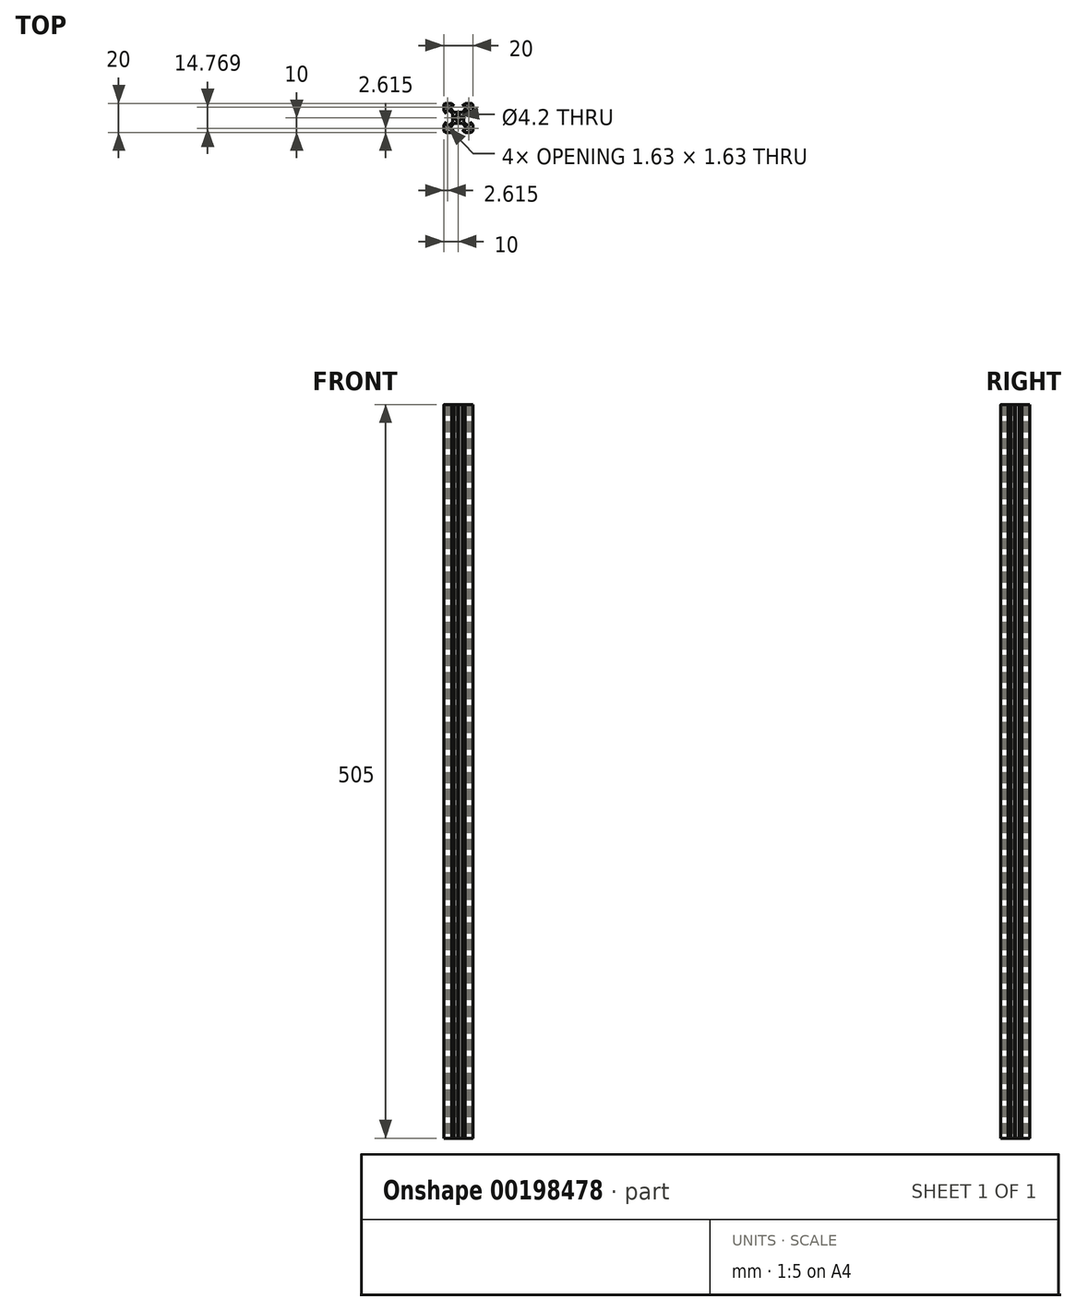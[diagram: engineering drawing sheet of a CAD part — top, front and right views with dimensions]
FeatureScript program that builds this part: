
annotation { "Feature Type Name" : "Feature", "Feature Type Description" : "" }
export const myFeature = defineFeature(function(context is Context, id is Id, definition is map)
    precondition{}
    {
        {
            var Q0;
            Q0=qCreatedBy(makeId("Top.planeOp"),FACE);
            var sketch = newSketch(context, id + "F0", { "sketchPlane" : qUnion([Q0])});
            skLineSegment(sketch, "E0", {"start": v(10, 8.5) * mm, "end": v(10, 4.64) * mm});
            skLineSegment(sketch, "E1", {"start": v(8.5, -10) * mm, "end": v(4.64, -10) * mm});
            skLineSegment(sketch, "E2", {"start": v(-10, -8.5) * mm, "end": v(-10, -4.64) * mm});
            skLineSegment(sketch, "E3", {"start": v(-8.5, 10) * mm, "end": v(-4.64, 10) * mm});
            skLineSegment(sketch, "E4.0", {"start": v(-5.5, 8.2) * mm, "end": v(-2.84, 8.2) * mm});
            skLineSegment(sketch, "E4.1", {"start": v(-8.2, -5.5) * mm, "end": v(-8.2, -2.84) * mm});
            skLineSegment(sketch, "E4.2", {"start": v(5.5, -8.2) * mm, "end": v(2.84, -8.2) * mm});
            skLineSegment(sketch, "E4.3", {"start": v(8.2, 5.5) * mm, "end": v(8.2, 2.84) * mm});
            skLineSegment(sketch, "E5.trimOffspring", {"start": v(4.64, 10) * mm, "end": v(8.5, 10) * mm});
            skPoint(sketch, "E6.start.orphan", {"position": v(0, 10) * mm});
            skLineSegment(sketch, "E7", {"start": v(-2.84, 8.2) * mm, "end": v(-4.64, 10) * mm});
            skLineSegment(sketch, "E8.trimOffspring", {"start": v(2.84, 8.2) * mm, "end": v(5.5, 8.2) * mm});
            skLineSegment(sketch, "E9.MirrorCS", {"start": v(2.84, 8.2) * mm, "end": v(4.64, 10) * mm});
            skLineSegment(sketch, "E10.MirrorCS", {"start": v(2.84, -8.2) * mm, "end": v(4.64, -10) * mm});
            skLineSegment(sketch, "E11.MirrorCS", {"start": v(-2.84, -8.2) * mm, "end": v(-4.64, -10) * mm});
            skLineSegment(sketch, "E12.trimOffspring", {"start": v(-2.84, -8.2) * mm, "end": v(-5.5, -8.2) * mm});
            skLineSegment(sketch, "E13.trimOffspring", {"start": v(-4.64, -10) * mm, "end": v(-8.5, -10) * mm});
            skLineSegment(sketch, "E14", {"start": v(-8.2, 2.84) * mm, "end": v(-10, 4.64) * mm});
            skLineSegment(sketch, "E15", {"start": v(-8.2, -2.84) * mm, "end": v(-10, -4.64) * mm});
            skLineSegment(sketch, "E16.trimOffspring", {"start": v(-10, 4.64) * mm, "end": v(-10, 8.5) * mm});
            skLineSegment(sketch, "E17.trimOffspring", {"start": v(-8.2, 2.84) * mm, "end": v(-8.2, 5.5) * mm});
            skLineSegment(sketch, "E18.MirrorCS", {"start": v(8.2, 2.84) * mm, "end": v(10, 4.64) * mm});
            skLineSegment(sketch, "E19.MirrorCS", {"start": v(8.2, -2.84) * mm, "end": v(10, -4.64) * mm});
            skLineSegment(sketch, "E20.trimOffspring", {"start": v(8.2, -2.84) * mm, "end": v(8.2, -5.5) * mm});
            skLineSegment(sketch, "E21.trimOffspring", {"start": v(10, -4.64) * mm, "end": v(10, -8.5) * mm});
            skCircle(sketch, "E22", {"center": v(0, 0) * mm, "radius": 2.1 * mm});
            skLineSegment(sketch, "E23", {"start": v(-6.56, 5.5) * mm, "end": v(-3.9, 2.84) * mm});
            skLineSegment(sketch, "E24", {"start": v(-5.5, 6.56) * mm, "end": v(-2.84, 3.9) * mm});
            skLineSegment(sketch, "E25", {"start": v(-5.5, 6.56) * mm, "end": v(-5.5, 8.2) * mm});
            skLineSegment(sketch, "E26", {"start": v(-6.56, 5.5) * mm, "end": v(-8.2, 5.5) * mm});
            skLineSegment(sketch, "E27", {"start": v(6.56, 5.5) * mm, "end": v(3.9, 2.84) * mm});
            skLineSegment(sketch, "E28", {"start": v(5.5, 6.56) * mm, "end": v(2.84, 3.9) * mm});
            skLineSegment(sketch, "E29", {"start": v(-6.56, -5.5) * mm, "end": v(-8.2, -5.5) * mm});
            skLineSegment(sketch, "E30", {"start": v(-5.5, -6.56) * mm, "end": v(-5.5, -8.2) * mm});
            skLineSegment(sketch, "E31", {"start": v(5.5, 6.56) * mm, "end": v(5.5, 8.2) * mm});
            skLineSegment(sketch, "E32", {"start": v(6.56, 5.5) * mm, "end": v(8.2, 5.5) * mm});
            skLineSegment(sketch, "E33", {"start": v(5.5, -6.56) * mm, "end": v(5.5, -8.2) * mm});
            skLineSegment(sketch, "E34", {"start": v(6.56, -5.5) * mm, "end": v(8.2, -5.5) * mm});
            skLineSegment(sketch, "E35.trimOffspring", {"start": v(2.84, -3.9) * mm, "end": v(5.5, -6.56) * mm});
            skLineSegment(sketch, "E36.trimOffspring", {"start": v(-2.84, -3.9) * mm, "end": v(-5.5, -6.56) * mm});
            skLineSegment(sketch, "E37.trimOffspring", {"start": v(-3.9, -2.84) * mm, "end": v(-6.56, -5.5) * mm});
            skLineSegment(sketch, "E38.trimOffspring", {"start": v(3.9, -2.84) * mm, "end": v(6.56, -5.5) * mm});
            skLineSegment(sketch, "E39", {"start": v(-3.9, -2.84) * mm, "end": v(-3.9, -0.25) * mm});
            skLineSegment(sketch, "E40", {"start": v(-2.84, 3.9) * mm, "end": v(-0.25, 3.9) * mm});
            skLineSegment(sketch, "E41", {"start": v(-2.84, -3.9) * mm, "end": v(-0.25, -3.9) * mm});
            skLineSegment(sketch, "E42", {"start": v(3.9, 2.84) * mm, "end": v(3.9, 0.25) * mm});
            skLineSegment(sketch, "E43", {"start": v(-8.2, 6.57) * mm, "end": v(-8.2, 8.2) * mm});
            skLineSegment(sketch, "E44", {"start": v(-6.57, 8.2) * mm, "end": v(-8.2, 8.2) * mm});
            skLineSegment(sketch, "E45", {"start": v(-8.2, 6.57) * mm, "end": v(-7.63, 6.57) * mm});
            skLineSegment(sketch, "E46", {"start": v(-6.57, 8.2) * mm, "end": v(-6.57, 7.63) * mm});
            skLineSegment(sketch, "E47", {"start": v(-7.63, 6.57) * mm, "end": v(-6.57, 7.63) * mm});
            skLineSegment(sketch, "E48.MirrorCS", {"start": v(6.57, 8.2) * mm, "end": v(8.2, 8.2) * mm});
            skLineSegment(sketch, "E49.MirrorCS", {"start": v(8.2, 6.57) * mm, "end": v(8.2, 8.2) * mm});
            skLineSegment(sketch, "E50.MirrorCS", {"start": v(8.2, 6.57) * mm, "end": v(7.63, 6.57) * mm});
            skLineSegment(sketch, "E51.MirrorCS", {"start": v(7.63, 6.57) * mm, "end": v(6.57, 7.63) * mm});
            skLineSegment(sketch, "E52.MirrorCS", {"start": v(6.57, 8.2) * mm, "end": v(6.57, 7.63) * mm});
            skLineSegment(sketch, "E53.MirrorCS", {"start": v(6.57, -8.2) * mm, "end": v(6.57, -7.63) * mm});
            skLineSegment(sketch, "E54.MirrorCS", {"start": v(8.2, -6.57) * mm, "end": v(7.63, -6.57) * mm});
            skLineSegment(sketch, "E55.MirrorCS", {"start": v(7.63, -6.57) * mm, "end": v(6.57, -7.63) * mm});
            skLineSegment(sketch, "E56.MirrorCS", {"start": v(6.57, -8.2) * mm, "end": v(8.2, -8.2) * mm});
            skLineSegment(sketch, "E57.MirrorCS", {"start": v(8.2, -6.57) * mm, "end": v(8.2, -8.2) * mm});
            skLineSegment(sketch, "E58.MirrorCS", {"start": v(-6.57, -8.2) * mm, "end": v(-8.2, -8.2) * mm});
            skLineSegment(sketch, "E59.MirrorCS", {"start": v(-8.2, -6.57) * mm, "end": v(-7.63, -6.57) * mm});
            skLineSegment(sketch, "E60.MirrorCS", {"start": v(-8.2, -6.57) * mm, "end": v(-8.2, -8.2) * mm});
            skLineSegment(sketch, "E61.MirrorCS", {"start": v(-7.63, -6.57) * mm, "end": v(-6.57, -7.63) * mm});
            skLineSegment(sketch, "E62.MirrorCS", {"start": v(-6.57, -8.2) * mm, "end": v(-6.57, -7.63) * mm});
            skPoint(sketch, "E63.visualSharp", {"position": v(-10, 10) * mm});
            skArc(sketch, "E63.filletArc", {"start": v(-8.5, 10) * mm, "mid": v(-9.56, 9.56) * mm, "end": v(-10, 8.5) * mm});
            skPoint(sketch, "E64.visualSharp", {"position": v(10, 10) * mm});
            skArc(sketch, "E64.filletArc", {"start": v(10, 8.5) * mm, "mid": v(9.56, 9.56) * mm, "end": v(8.5, 10) * mm});
            skPoint(sketch, "E65.visualSharp", {"position": v(10, -10) * mm});
            skArc(sketch, "E65.filletArc", {"start": v(8.5, -10) * mm, "mid": v(9.56, -9.56) * mm, "end": v(10, -8.5) * mm});
            skPoint(sketch, "E66.visualSharp", {"position": v(-10, -10) * mm});
            skArc(sketch, "E66.filletArc", {"start": v(-10, -8.5) * mm, "mid": v(-9.56, -9.56) * mm, "end": v(-8.5, -10) * mm});
            skLineSegment(sketch, "E67", {"start": v(-3.65, 0) * mm, "end": v(-3.9, 0.25) * mm});
            skLineSegment(sketch, "E68.MirrorCS", {"start": v(-3.65, 0) * mm, "end": v(-3.9, -0.25) * mm});
            skLineSegment(sketch, "E69.trimOffspring", {"start": v(-3.9, 0.25) * mm, "end": v(-3.9, 2.84) * mm});
            skLineSegment(sketch, "E70.MirrorCS", {"start": v(3.65, 0) * mm, "end": v(3.9, 0.25) * mm});
            skLineSegment(sketch, "E71.MirrorCS", {"start": v(3.65, 0) * mm, "end": v(3.9, -0.25) * mm});
            skLineSegment(sketch, "E72", {"start": v(0, -3.65) * mm, "end": v(0.25, -3.9) * mm});
            skLineSegment(sketch, "E73.MirrorCS", {"start": v(0, -3.65) * mm, "end": v(-0.25, -3.9) * mm});
            skLineSegment(sketch, "E74.trimOffspring", {"start": v(0.25, -3.9) * mm, "end": v(2.84, -3.9) * mm});
            skLineSegment(sketch, "E75.trimOffspring", {"start": v(3.9, -0.25) * mm, "end": v(3.9, -2.84) * mm});
            skLineSegment(sketch, "E76.MirrorCS", {"start": v(0, 3.65) * mm, "end": v(-0.25, 3.9) * mm});
            skLineSegment(sketch, "E77.MirrorCS", {"start": v(0, 3.65) * mm, "end": v(0.25, 3.9) * mm});
            skLineSegment(sketch, "E78.trimOffspring", {"start": v(0.25, 3.9) * mm, "end": v(2.84, 3.9) * mm});
            skSolve(sketch);
        }
        {
            var Q0;
            Q0=makeQuery(id+"F0.imprint","IMPRINT",FACE,{"disambiguationData":[TD([[makeQuery(id+"F0.imprint","IMPRINT",EDGE,{"derivedFrom":sQuery(id+"F0.wireOp",EDGE,"E0")}),-1.0]])]});
            extrude(context, id + "F1", {"entities" : qUnion([Q0]), "depth" : 505 * mm});
        }
    });
